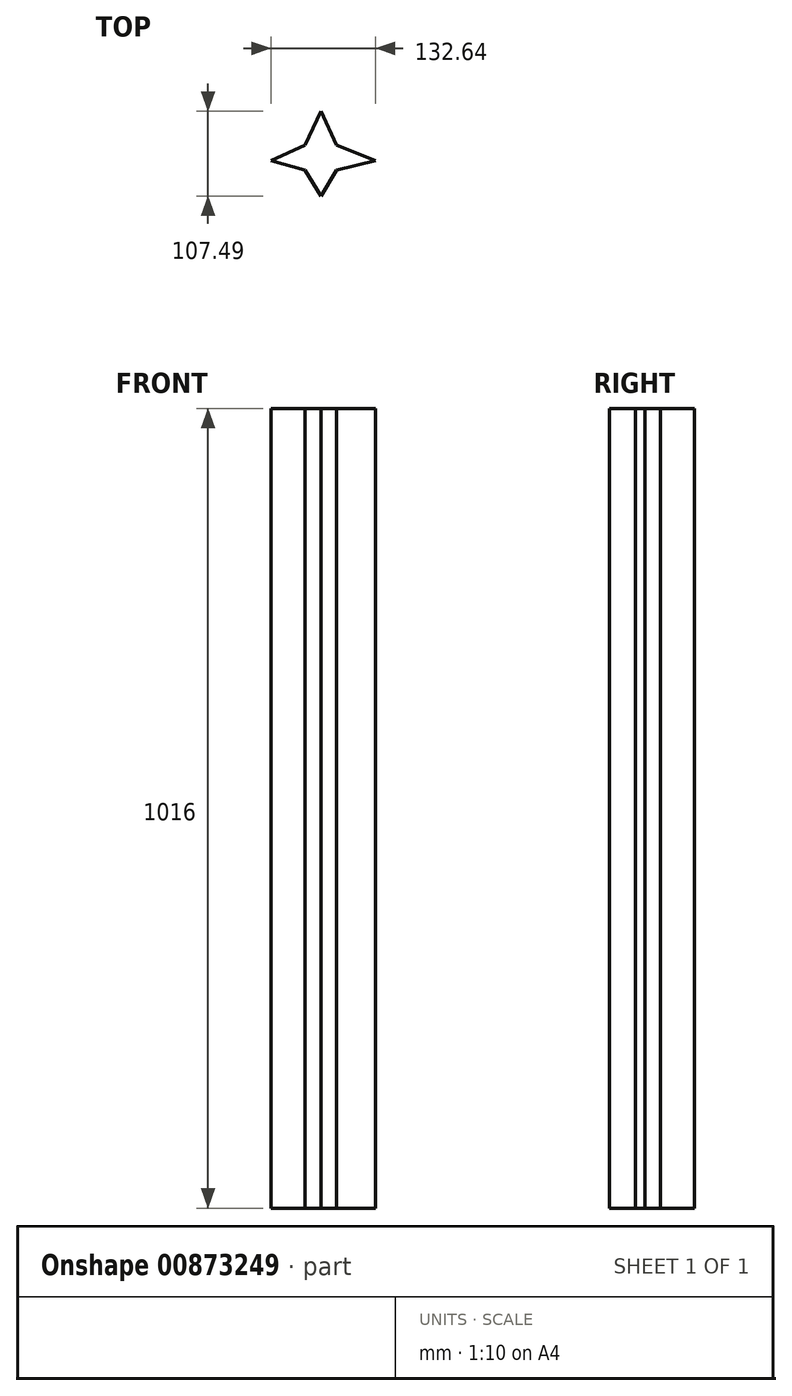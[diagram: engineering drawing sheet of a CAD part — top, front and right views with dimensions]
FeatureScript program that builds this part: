
annotation { "Feature Type Name" : "Feature", "Feature Type Description" : "" }
export const myFeature = defineFeature(function(context is Context, id is Id, definition is map)
    precondition{}
    {
        {
            var Q0;
            Q0=qCreatedBy(makeId("Top.planeOp"),FACE);
            var sketch = newSketch(context, id + "F0", { "sketchPlane" : qUnion([Q0])});
            skLineSegment(sketch, "E0", {"start": v(0, 62.47) * mm, "end": v(19.17, 19.47) * mm});
            skLineSegment(sketch, "E1", {"start": v(19.17, 19.47) * mm, "end": v(69.06, 0) * mm});
            skLineSegment(sketch, "E2", {"start": v(69.06, 0) * mm, "end": v(19.17, -12.17) * mm});
            skLineSegment(sketch, "E3", {"start": v(19.17, -12.17) * mm, "end": v(0, -45.02) * mm});
            skLineSegment(sketch, "E4", {"start": v(0, -45.02) * mm, "end": v(-20.38, -12.17) * mm});
            skLineSegment(sketch, "E5", {"start": v(-20.38, -12.17) * mm, "end": v(-63.58, 0) * mm});
            skLineSegment(sketch, "E6", {"start": v(-63.58, 0) * mm, "end": v(-20.59, 19.47) * mm});
            skLineSegment(sketch, "E7", {"start": v(-20.59, 19.47) * mm, "end": v(0, 62.47) * mm});
            skSolve(sketch);
        }
        {
            var Q0;
            Q0 = qSketchRegion(id + "F0", true);
            extrude(context, id + "F1", {"entities" : qUnion([Q0]), "depth" : 1016 * mm, "offsetDistance" : 25.4 * mm});
        }
    });
